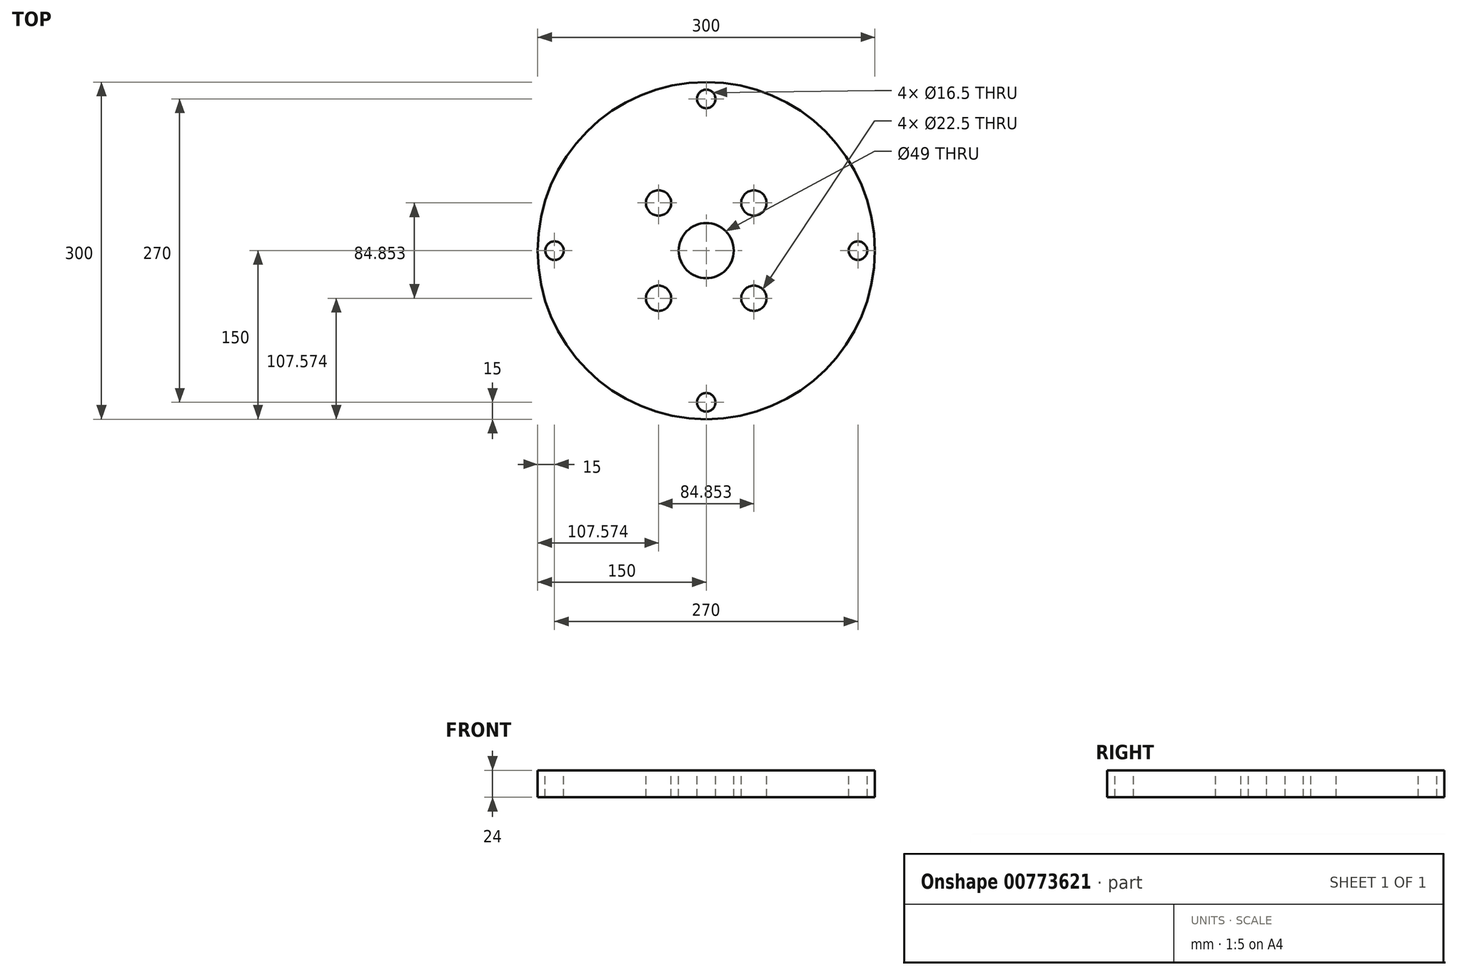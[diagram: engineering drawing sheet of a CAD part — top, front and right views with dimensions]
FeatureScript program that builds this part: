
annotation { "Feature Type Name" : "Feature", "Feature Type Description" : "" }
export const myFeature = defineFeature(function(context is Context, id is Id, definition is map)
    precondition{}
    {
        {
            var Q0;
            Q0=qCreatedBy(makeId("Top.planeOp"),FACE);
            var sketch = newSketch(context, id + "F0", { "sketchPlane" : qUnion([Q0])});
            skCircle(sketch, "E0", {"center": v(0, 0) * mm, "radius": 150 * mm});
            skCircle(sketch, "E1", {"center": v(0, 0) * mm, "radius": 24.5 * mm});
            skCircle(sketch, "E2", {"center": v(0, 0) * mm, "radius": 60 * mm, "construction": true});
            skCircle(sketch, "E3", {"center": v(0, 0) * mm, "radius": 135 * mm, "construction": true});
            skCircle(sketch, "E4", {"center": v(0, 135) * mm, "radius": 8.25 * mm});
            skCircle(sketch, "E5.1.0", {"center": v(-135, 0) * mm, "radius": 8.25 * mm});
            skCircle(sketch, "E5.2.0", {"center": v(0, -135) * mm, "radius": 8.25 * mm});
            skCircle(sketch, "E5.3.0", {"center": v(135, 0) * mm, "radius": 8.25 * mm});
            skLineSegment(sketch, "E6", {"start": v(0, 0) * mm, "end": v(-122.16, 122.16) * mm, "construction": true});
            skCircle(sketch, "E7", {"center": v(-42.43, 42.43) * mm, "radius": 11.25 * mm});
            skCircle(sketch, "E8.1.0", {"center": v(-42.43, -42.43) * mm, "radius": 11.25 * mm});
            skCircle(sketch, "E8.2.0", {"center": v(42.43, -42.43) * mm, "radius": 11.25 * mm});
            skCircle(sketch, "E8.3.0", {"center": v(42.43, 42.43) * mm, "radius": 11.25 * mm});
            skSolve(sketch);
        }
        {
            var Q0;
            Q0=makeQuery(id+"F0.imprint","IMPRINT",FACE,{"disambiguationData":[TD([[makeQuery(id+"F0.imprint","IMPRINT",EDGE,{"derivedFrom":sQuery(id+"F0.wireOp",EDGE,"E0")}),1.0]])]});
            extrude(context, id + "F1", {"entities" : qUnion([Q0]), "oppositeDirection" : true, "depth" : 24 * mm, "offsetDistance" : 25 * mm});
        }
    });
